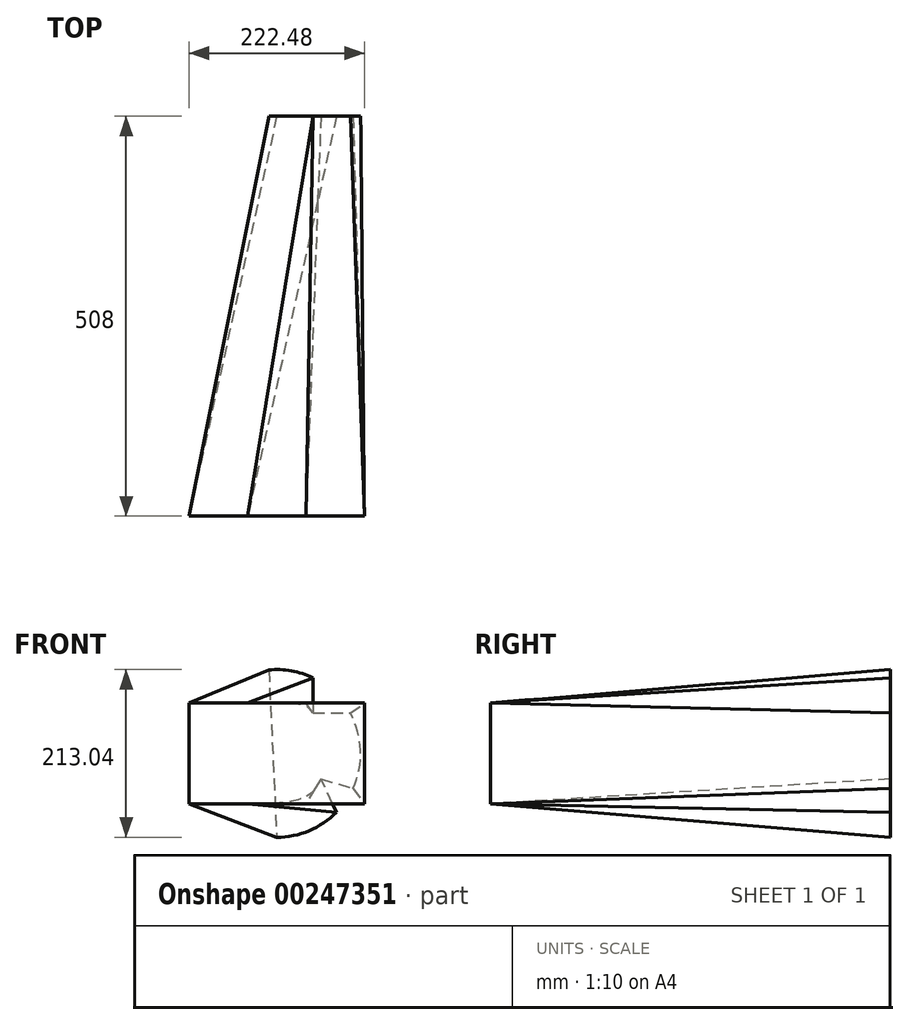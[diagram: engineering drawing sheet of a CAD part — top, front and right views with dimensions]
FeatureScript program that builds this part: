
annotation { "Feature Type Name" : "Feature", "Feature Type Description" : "" }
export const myFeature = defineFeature(function(context is Context, id is Id, definition is map)
    precondition{}
    {
        {
            var Q0;
            Q0=qCreatedBy(makeId("Front.planeOp"),FACE);
            var sketch = newSketch(context, id + "F0", { "sketchPlane" : qUnion([Q0])});
            skArc(sketch, "E0", {"start": v(0, -106.52) * mm, "mid": v(41.2, -98.23) * mm, "end": v(75.98, -74.65) * mm});
            skLineSegment(sketch, "E1", {"start": v(-10.11, 106.04) * mm, "end": v(0, -106.52) * mm});
            skLineSegment(sketch, "E2.top", {"start": v(45.84, 51.22) * mm, "end": v(93.4, 51.22) * mm});
            skLineSegment(sketch, "E2.left", {"start": v(45.84, 96.16) * mm, "end": v(45.84, 51.22) * mm});
            skArc(sketch, "E3.trimOffspring", {"start": v(45.84, 96.16) * mm, "mid": v(18.53, 104.9) * mm, "end": v(-10.11, 106.04) * mm});
            skLineSegment(sketch, "E4", {"start": v(75.98, -74.65) * mm, "end": v(56.06, -32.4) * mm});
            skLineSegment(sketch, "E5", {"start": v(56.06, -32.4) * mm, "end": v(96.82, -44.4) * mm});
            skArc(sketch, "E6.trimOffspring", {"start": v(96.82, -44.4) * mm, "mid": v(106.45, 3.82) * mm, "end": v(93.4, 51.22) * mm});
            skSolve(sketch);
        }
        {
            var Q0;
            Q0=qCreatedBy(makeId("Front.planeOp"),FACE);
            cPlane(context, id + "F1", {"entities" : qUnion([Q0]), "cplaneType" : CPlaneType.OFFSET, "offset" : 508 * mm, "width" : 152.4 * mm, "height" : 152.4 * mm});
        }
        {
            var Q0;
            Q0=qCreatedBy(id+"F1.planeOp",FACE);
            var sketch = newSketch(context, id + "F2", { "sketchPlane" : qUnion([Q0])});
            skLineSegment(sketch, "E7.bottom", {"start": v(111.24, -64) * mm, "end": v(-111.24, -64) * mm});
            skLineSegment(sketch, "E7.top", {"start": v(111.24, 64) * mm, "end": v(-111.24, 64) * mm});
            skLineSegment(sketch, "E7.left", {"start": v(111.24, -64) * mm, "end": v(111.24, 64) * mm});
            skLineSegment(sketch, "E7.right", {"start": v(-111.24, -64) * mm, "end": v(-111.24, 64) * mm});
            skPoint(sketch, "E7.middle", {"position": v(0, 0) * mm});
            skSolve(sketch);
        }
        {
            var Q0;
            Q0=makeQuery(id+"F0.imprint","IMPRINT",FACE,{"disambiguationData":[TD([[makeQuery(id+"F0.imprint","IMPRINT",EDGE,{"derivedFrom":sQuery(id+"F0.wireOp",EDGE,"E0")}),1.0]])]});
            var Q1;
            Q1=makeQuery(id+"F2.imprint","IMPRINT",FACE,{"disambiguationData":[TD([[makeQuery(id+"F2.imprint","IMPRINT",EDGE,{"derivedFrom":sQuery(id+"F2.wireOp",EDGE,"E7.bottom")}),-1.0]])]});
            loft(context, id + "F3", {"sheetProfilesArray" : [{ "sheetProfileEntities" : qUnion([Q0]) }, { "sheetProfileEntities" : qUnion([Q1]) }]});
        }
    });
